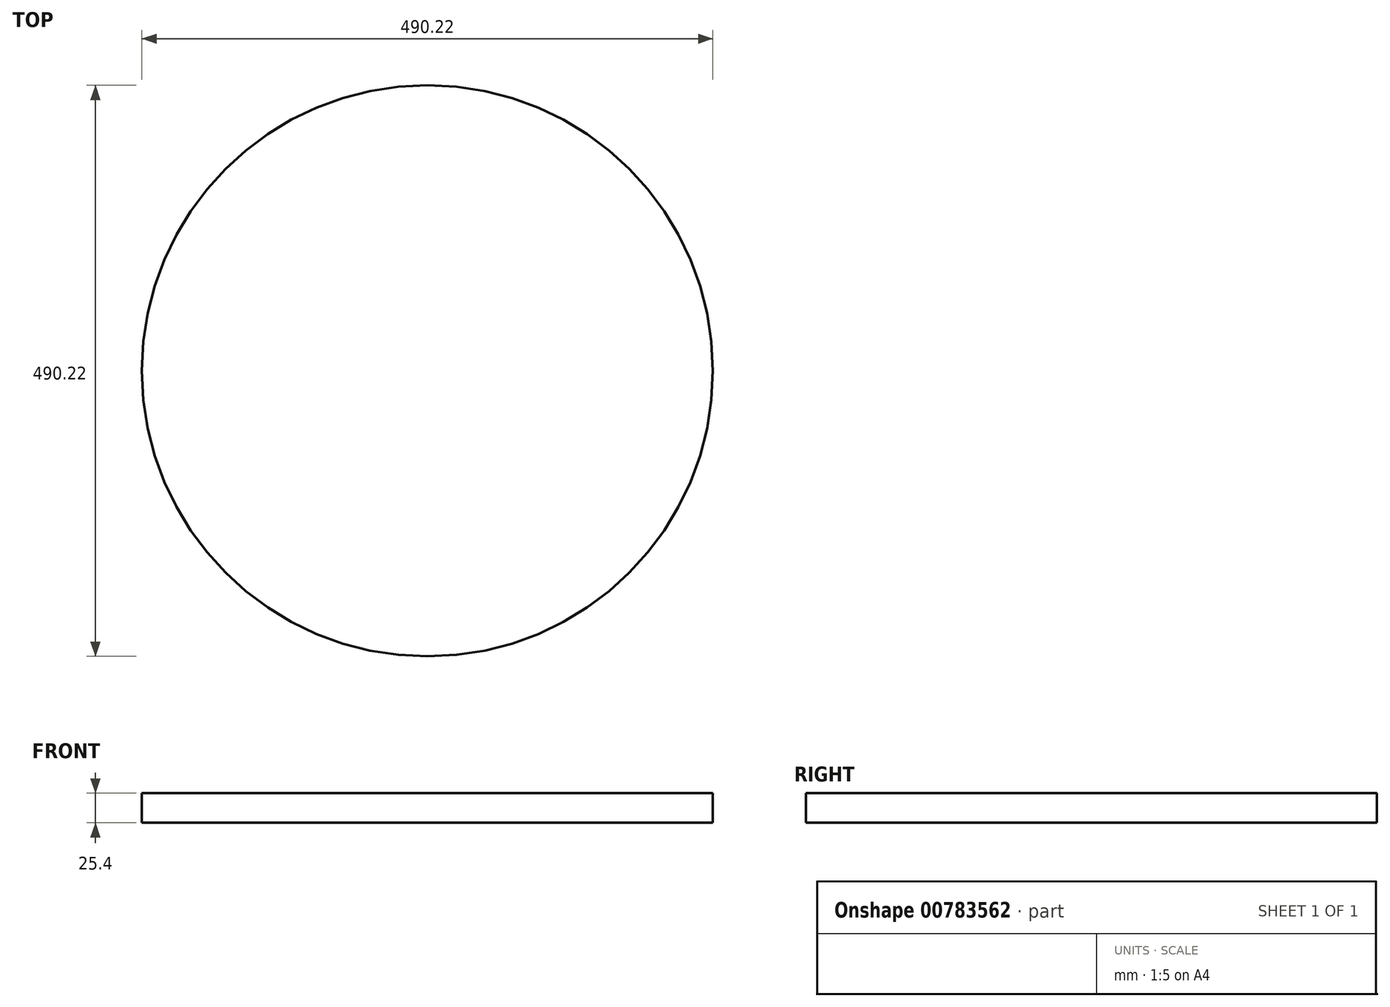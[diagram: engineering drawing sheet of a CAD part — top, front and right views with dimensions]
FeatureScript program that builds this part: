
annotation { "Feature Type Name" : "Feature", "Feature Type Description" : "" }
export const myFeature = defineFeature(function(context is Context, id is Id, definition is map)
    precondition{}
    {
        {
            var Q0;
            Q0=qCreatedBy(makeId("Top.planeOp"),FACE);
            var sketch = newSketch(context, id + "F0", { "sketchPlane" : qUnion([Q0])});
            skCircle(sketch, "E0", {"center": v(0, 0) * mm, "radius": 245.1 * mm});
            skSolve(sketch);
        }
        {
            var Q0;
            Q0 = qSketchRegion(id + "F0", true);
            extrude(context, id + "F1", {"entities" : qUnion([Q0]), "depth" : 25.4 * mm, "offsetDistance" : 25.4 * mm});
        }
    });
